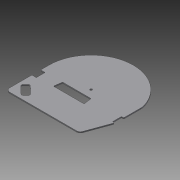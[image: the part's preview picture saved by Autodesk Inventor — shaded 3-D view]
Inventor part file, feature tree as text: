
AUTODESK INVENTOR PART (.ipt)
format: ipt  version: 2015 (Build 190159000, 159)  size: 167,424 bytes
history: native  units: mm
features: fillet x5, extrude x3, sketch x3, chamfer x2
ambient origin geometry x8: Origin, YZ Plane, XZ Plane, XY Plane, X Axis, Y Axis, Z Axis, Center Point
bodies: Solid1 (feature_tree)
feature tree (13):
  extrude  "Extrusion1"  Depth=57.0mm
  fillet  "Fillet1"  Radius=20.0mm
  fillet  "Fillet2"  Radius=6.0mm
  fillet  "Fillet3"  Radius=12.0mm
  extrude  "Extrusion2"  Depth=3.0mm
  chamfer  "Chamfer1"  Distance=99.0mm
  chamfer  "Chamfer2"  Distance=47.0mm
  fillet  "Fillet4"  Radius=58.0mm
  extrude  "Extrusion3"  Depth=1.5mm TaperAngle=0.0deg
  fillet  "Fillet5"  Radius=0.5mm
  sketch  "Sketch1"  dims[d0=3.0mm d1=57.0mm d2=20.0mm d3=6.0mm d4=12.0mm]
  sketch  "Sketch2"  dims[d5=55.0mm d6=3.0mm]
  sketch  "Sketch3"  dims[d7=19.198622mm d8=99.0mm d9=47.0mm d10=58.0mm d11=1.5mm d12=0.0mm d13=0.5mm d14=1.0mm d15=5.0mm d16=41.5mm d17=11.0mm d18=9.0mm d19=12.0mm d20=1.5mm d21=0.0mm d22=11.0mm d23=1.5mm d24=45.0deg d25=11.0mm d26=1.5mm d27=45.0deg d28=1.0mm d29=103.0mm d30=18.0mm d31=9.0mm d32=58.0mm d33=1.5mm d34=0.0mm d35=2.0mm]
